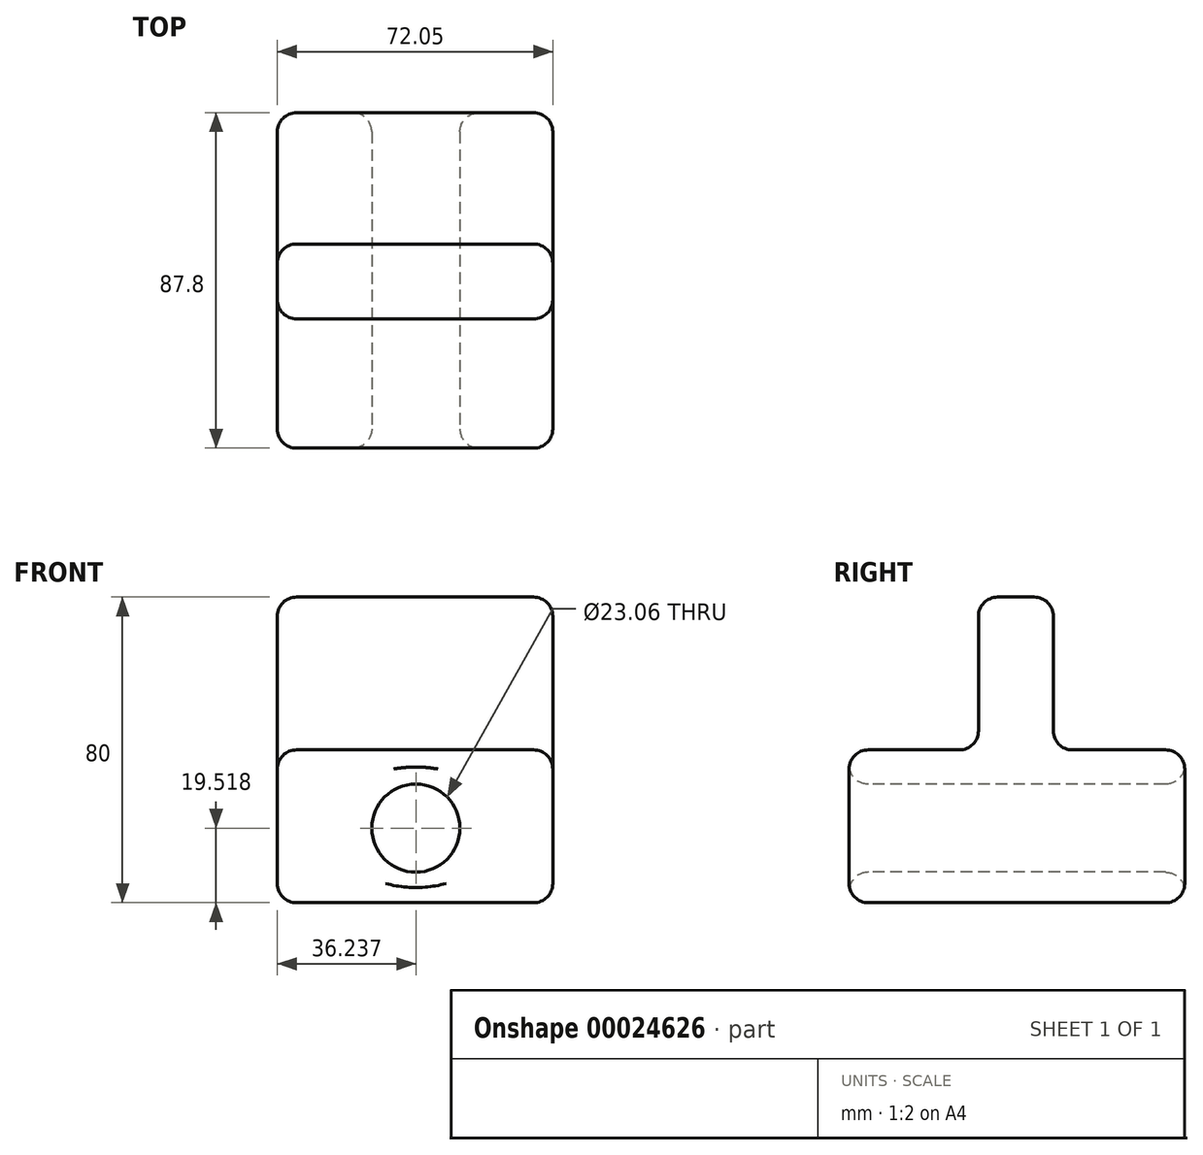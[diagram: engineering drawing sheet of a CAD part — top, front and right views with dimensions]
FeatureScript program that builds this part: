
annotation { "Feature Type Name" : "Feature", "Feature Type Description" : "" }
export const myFeature = defineFeature(function(context is Context, id is Id, definition is map)
    precondition{}
    {
        {
            var Q0;
            Q0=qCreatedBy(makeId("Top.planeOp"),FACE);
            var sketch = newSketch(context, id + "F0", { "sketchPlane" : qUnion([Q0])});
            skLineSegment(sketch, "E0.bottom", {"start": v(-59.89, -44.54) * mm, "end": v(12.16, -44.54) * mm});
            skLineSegment(sketch, "E0.top", {"start": v(-59.89, 43.26) * mm, "end": v(12.16, 43.26) * mm});
            skLineSegment(sketch, "E0.left", {"start": v(-59.89, -44.54) * mm, "end": v(-59.89, 43.26) * mm});
            skLineSegment(sketch, "E0.right", {"start": v(12.16, -44.54) * mm, "end": v(12.16, 43.26) * mm});
            skSolve(sketch);
        }
        {
            var Q0;
            Q0=makeQuery(id+"F0.imprint","IMPRINT",FACE,{"disambiguationData":[TD([[makeQuery(id+"F0.imprint","IMPRINT",EDGE,{"derivedFrom":sQuery(id+"F0.wireOp",EDGE,"E0.bottom")}),1.0]])]});
            extrude(context, id + "F1", {"entities" : qUnion([Q0]), "depth" : 40 * mm});
        }
        {
            var Q0;
            Q0=makeQuery(id+"F1.opExtrude","SWEPT_FACE",FACE,{"disambiguationData":[OSD([sQuery(id+"F0.wireOp",EDGE,"E0.bottom")])]});
            var sketch = newSketch(context, id + "F2", { "sketchPlane" : qUnion([Q0])});
            skCircle(sketch, "E1", {"center": v(-23.65, 19.52) * mm, "radius": 11.53 * mm});
            skSolve(sketch);
        }
        {
            var Q0;
            Q0=makeQuery(id+"F2.imprint","IMPRINT",FACE,{"disambiguationData":[TD([[makeQuery(id+"F2.imprint","IMPRINT",EDGE,{"derivedFrom":sQuery(id+"F2.wireOp",EDGE,"E1")}),1.0]])]});
            extrude(context, id + "F3", {"entities" : qUnion([Q0]), "operationType" : NewBodyOperationType.REMOVE, "endBound" : BoundingType.THROUGH_ALL, "oppositeDirection" : true, "depth" : 25 * mm});
        }
        {
            var Q0;
            Q0=makeQuery(id+"F1.opExtrude","CAP_FACE",FACE,{"disambiguationData":[OSD([sQuery(id+"F0.wireOp",EDGE,"E0.bottom"),sQuery(id+"F0.wireOp",EDGE,"E0.top"),sQuery(id+"F0.wireOp",EDGE,"E0.left"),sQuery(id+"F0.wireOp",EDGE,"E0.right")])],"isStart":false});
            var sketch = newSketch(context, id + "F4", { "sketchPlane" : qUnion([Q0])});
            skLineSegment(sketch, "E2.bottom", {"start": v(-59.89, -10.7) * mm, "end": v(12.16, -10.7) * mm});
            skLineSegment(sketch, "E2.top", {"start": v(-59.89, 8.88) * mm, "end": v(12.16, 8.88) * mm});
            skLineSegment(sketch, "E2.left", {"start": v(-59.89, -10.7) * mm, "end": v(-59.89, 8.88) * mm});
            skLineSegment(sketch, "E2.right", {"start": v(12.16, -10.7) * mm, "end": v(12.16, 8.88) * mm});
            skSolve(sketch);
        }
        {
            var Q0;
            Q0=makeQuery(id+"F4.imprint","IMPRINT",FACE,{"disambiguationData":[TD([[makeQuery(id+"F4.imprint","IMPRINT",EDGE,{"derivedFrom":sQuery(id+"F4.wireOp",EDGE,"E2.bottom")}),1.0]])]});
            extrude(context, id + "F5", {"entities" : qUnion([Q0]), "operationType" : NewBodyOperationType.ADD, "depth" : 40 * mm});
        }
        {
            var Q0;
            Q0=makeQuery(id+"F3.boolean.opBoolean","COPY",FACE,{"derivedFrom":makeQuery(id+"F3.opExtrude","SWEPT_FACE",FACE,{"disambiguationData":[OSD([sQuery(id+"F2.wireOp",EDGE,"E1")])]})});
            var Q1;
            Q1=makeQuery(id+"F1.opExtrude","SWEPT_FACE",FACE,{"disambiguationData":[OSD([sQuery(id+"F0.wireOp",EDGE,"E0.bottom")])]});
            var Q2;
            Q2=makeQuery(id+"F3.boolean.opBoolean","COPY",EDGE,{"derivedFrom":makeQuery(id+"F3.opExtrude","CAP_EDGE",EDGE,{"disambiguationData":[OSD([sQuery(id+"F2.wireOp",EDGE,"E1")])],"isStart":true})});
            var Q3;
            Q3=makeQuery(id+"F5.opExtrude","SWEPT_EDGE",EDGE,{"disambiguationData":[OSD([sQuery(id+"F0.wireOp",EDGE,"E0.left"),sQuery(id+"F4.wireOp",EDGE,"E2.bottom"),sQuery(id+"F4.wireOp",EDGE,"E2.left")])]});
            var Q4;
            Q4=makeQuery(id+"F5.opExtrude","SWEPT_FACE",FACE,{"disambiguationData":[OSD([sQuery(id+"F4.wireOp",EDGE,"E2.bottom")])]});
            var Q5;
            Q5=makeQuery(id+"F5.opExtrude","SWEPT_EDGE",EDGE,{"disambiguationData":[OSD([sQuery(id+"F0.wireOp",EDGE,"E0.right"),sQuery(id+"F4.wireOp",EDGE,"E2.bottom"),sQuery(id+"F4.wireOp",EDGE,"E2.right")])]});
            var Q6;
            Q6=makeQuery(id+"F5.opExtrude","CAP_FACE",FACE,{"disambiguationData":[OSD([sQuery(id+"F4.wireOp",EDGE,"E2.bottom"),sQuery(id+"F4.wireOp",EDGE,"E2.top"),sQuery(id+"F4.wireOp",EDGE,"E2.left"),sQuery(id+"F4.wireOp",EDGE,"E2.right")])],"isStart":false});
            var Q7;
            Q7=makeQuery(id+"F5.opExtrude","SWEPT_EDGE",EDGE,{"disambiguationData":[OSD([sQuery(id+"F0.wireOp",EDGE,"E0.right"),sQuery(id+"F4.wireOp",EDGE,"E2.top"),sQuery(id+"F4.wireOp",EDGE,"E2.right")])]});
            var Q8;
            Q8=makeQuery(id+"F5.opExtrude","CAP_EDGE",EDGE,{"disambiguationData":[OSD([sQuery(id+"F4.wireOp",EDGE,"E2.bottom")])],"isStart":false});
            var Q9;
            Q9=makeQuery(id+"F5.opExtrude","CAP_EDGE",EDGE,{"disambiguationData":[OSD([sQuery(id+"F4.wireOp",EDGE,"E2.bottom")])],"isStart":true});
            var Q10;
            Q10=makeQuery(id+"F5.opExtrude","CAP_EDGE",EDGE,{"disambiguationData":[OSD([sQuery(id+"F4.wireOp",EDGE,"E2.top")])],"isStart":false});
            var Q11;
            Q11=makeQuery(id+"F5.boolean.opBoolean","MERGE",FACE,{"derivedFrom":[makeQuery(id+"F1.opExtrude","SWEPT_FACE",FACE,{"disambiguationData":[OSD([sQuery(id+"F0.wireOp",EDGE,"E0.right")])]}),makeQuery(id+"F5.opExtrude","SWEPT_FACE",FACE,{"disambiguationData":[OSD([sQuery(id+"F4.wireOp",EDGE,"E2.right")])]})]});
            var Q12;
            {var subQ0=sQuery(id+"F0.wireOp",EDGE,"E0.bottom");var subQ1=sQuery(id+"F0.wireOp",EDGE,"E0.left");var subQ2=sQuery(id+"F0.wireOp",EDGE,"E0.right");Q12=makeQuery(id+"F5.boolean.opBoolean","SPLIT",FACE,{"disambiguationData":[TD([makeQuery(id+"F1.opExtrude","SWEPT_FACE",FACE,{"disambiguationData":[OSD([subQ0])]})])],"derivedFrom":makeQuery(id+"F1.opExtrude","CAP_FACE",FACE,{"disambiguationData":[OSD([subQ0,sQuery(id+"F0.wireOp",EDGE,"E0.top"),subQ1,subQ2])],"isStart":false})});}
            var Q13;
            Q13=makeQuery(id+"F1.opExtrude","SWEPT_EDGE",EDGE,{"disambiguationData":[OSD([sQuery(id+"F0.wireOp",EDGE,"E0.bottom"),sQuery(id+"F0.wireOp",EDGE,"E0.left")])]});
            var Q14;
            {var subQ0=sQuery(id+"F0.wireOp",EDGE,"E0.left");var subQ1=sQuery(id+"F0.wireOp",EDGE,"E0.bottom");Q14=makeQuery(id+"F5.boolean.opBoolean","SPLIT",EDGE,{"disambiguationData":[TD([makeQuery(id+"F1.opExtrude","SWEPT_FACE",FACE,{"disambiguationData":[OSD([subQ1])]})])],"derivedFrom":makeQuery(id+"F1.opExtrude","CAP_EDGE",EDGE,{"disambiguationData":[OSD([subQ0])],"isStart":false})});}
            var Q15;
            Q15=makeQuery(id+"F5.opExtrude","CAP_EDGE",EDGE,{"disambiguationData":[OSD([sQuery(id+"F4.wireOp",EDGE,"E2.left")])],"isStart":false});
            var Q16;
            {var subQ0=sQuery(id+"F0.wireOp",EDGE,"E0.top");var subQ1=sQuery(id+"F0.wireOp",EDGE,"E0.left");var subQ2=sQuery(id+"F0.wireOp",EDGE,"E0.right");Q16=makeQuery(id+"F5.boolean.opBoolean","SPLIT",FACE,{"disambiguationData":[TD([makeQuery(id+"F1.opExtrude","SWEPT_FACE",FACE,{"disambiguationData":[OSD([subQ0])]})])],"derivedFrom":makeQuery(id+"F1.opExtrude","CAP_FACE",FACE,{"disambiguationData":[OSD([sQuery(id+"F0.wireOp",EDGE,"E0.bottom"),subQ0,subQ1,subQ2])],"isStart":false})});}
            var Q17;
            {var subQ0=sQuery(id+"F0.wireOp",EDGE,"E0.right");var subQ1=sQuery(id+"F0.wireOp",EDGE,"E0.bottom");Q17=makeQuery(id+"F5.boolean.opBoolean","SPLIT",EDGE,{"disambiguationData":[TD([makeQuery(id+"F1.opExtrude","SWEPT_FACE",FACE,{"disambiguationData":[OSD([subQ1])]})])],"derivedFrom":makeQuery(id+"F1.opExtrude","CAP_EDGE",EDGE,{"disambiguationData":[OSD([subQ0])],"isStart":false})});}
            var Q18;
            Q18=makeQuery(id+"F5.opExtrude","CAP_EDGE",EDGE,{"disambiguationData":[OSD([sQuery(id+"F4.wireOp",EDGE,"E2.right")])],"isStart":false});
            var Q19;
            Q19=makeQuery(id+"F1.opExtrude","SWEPT_EDGE",EDGE,{"disambiguationData":[OSD([sQuery(id+"F0.wireOp",EDGE,"E0.top"),sQuery(id+"F0.wireOp",EDGE,"E0.right")])]});
            var Q20;
            {var subQ0=sQuery(id+"F0.wireOp",EDGE,"E0.right");var subQ1=sQuery(id+"F0.wireOp",EDGE,"E0.top");Q20=makeQuery(id+"F5.boolean.opBoolean","SPLIT",EDGE,{"disambiguationData":[TD([makeQuery(id+"F1.opExtrude","SWEPT_FACE",FACE,{"disambiguationData":[OSD([subQ1])]})])],"derivedFrom":makeQuery(id+"F1.opExtrude","CAP_EDGE",EDGE,{"disambiguationData":[OSD([subQ0])],"isStart":false})});}
            var Q21;
            Q21=makeQuery(id+"F1.opExtrude","CAP_EDGE",EDGE,{"disambiguationData":[OSD([sQuery(id+"F0.wireOp",EDGE,"E0.bottom")])],"isStart":true});
            var Q22;
            Q22=makeQuery(id+"F1.opExtrude","CAP_EDGE",EDGE,{"disambiguationData":[OSD([sQuery(id+"F0.wireOp",EDGE,"E0.bottom")])],"isStart":false});
            var Q23;
            Q23=makeQuery(id+"F1.opExtrude","CAP_EDGE",EDGE,{"disambiguationData":[OSD([sQuery(id+"F0.wireOp",EDGE,"E0.top")])],"isStart":false});
            var Q24;
            Q24=makeQuery(id+"F1.opExtrude","CAP_EDGE",EDGE,{"disambiguationData":[OSD([sQuery(id+"F0.wireOp",EDGE,"E0.right")])],"isStart":true});
            var Q25;
            Q25=makeQuery(id+"F3.boolean.opBoolean","INTERSECT",EDGE,{"derivedFrom":[makeQuery(id+"F1.opExtrude","SWEPT_FACE",FACE,{"disambiguationData":[OSD([sQuery(id+"F0.wireOp",EDGE,"E0.top")])]}),makeQuery(id+"F3.opExtrude","SWEPT_FACE",FACE,{"disambiguationData":[OSD([sQuery(id+"F2.wireOp",EDGE,"E1")])]})]});
            var Q26;
            Q26=makeQuery(id+"F1.opExtrude","SWEPT_FACE",FACE,{"disambiguationData":[OSD([sQuery(id+"F0.wireOp",EDGE,"E0.top")])]});
            var Q27;
            Q27=makeQuery(id+"F5.opExtrude","SWEPT_EDGE",EDGE,{"disambiguationData":[OSD([sQuery(id+"F0.wireOp",EDGE,"E0.left"),sQuery(id+"F4.wireOp",EDGE,"E2.top"),sQuery(id+"F4.wireOp",EDGE,"E2.left")])]});
            var Q28;
            Q28=makeQuery(id+"F5.opExtrude","SWEPT_FACE",FACE,{"disambiguationData":[OSD([sQuery(id+"F4.wireOp",EDGE,"E2.top")])]});
            var Q29;
            Q29=makeQuery(id+"F5.boolean.opBoolean","MERGE",FACE,{"derivedFrom":[makeQuery(id+"F1.opExtrude","SWEPT_FACE",FACE,{"disambiguationData":[OSD([sQuery(id+"F0.wireOp",EDGE,"E0.left")])]}),makeQuery(id+"F5.opExtrude","SWEPT_FACE",FACE,{"disambiguationData":[OSD([sQuery(id+"F4.wireOp",EDGE,"E2.left")])]})]});
            var Q30;
            Q30=makeQuery(id+"F5.opExtrude","CAP_EDGE",EDGE,{"disambiguationData":[OSD([sQuery(id+"F4.wireOp",EDGE,"E2.top")])],"isStart":true});
            var Q31;
            Q31=makeQuery(id+"F1.opExtrude","CAP_FACE",FACE,{"disambiguationData":[OSD([sQuery(id+"F0.wireOp",EDGE,"E0.bottom"),sQuery(id+"F0.wireOp",EDGE,"E0.top"),sQuery(id+"F0.wireOp",EDGE,"E0.left"),sQuery(id+"F0.wireOp",EDGE,"E0.right")])],"isStart":true});
            var Q32;
            Q32=makeQuery(id+"F1.opExtrude","SWEPT_EDGE",EDGE,{"disambiguationData":[OSD([sQuery(id+"F0.wireOp",EDGE,"E0.bottom"),sQuery(id+"F0.wireOp",EDGE,"E0.right")])]});
            var Q33;
            Q33=makeQuery(id+"F1.opExtrude","CAP_EDGE",EDGE,{"disambiguationData":[OSD([sQuery(id+"F0.wireOp",EDGE,"E0.top")])],"isStart":true});
            var Q34;
            Q34=makeQuery(id+"F1.opExtrude","CAP_EDGE",EDGE,{"disambiguationData":[OSD([sQuery(id+"F0.wireOp",EDGE,"E0.left")])],"isStart":true});
            var Q35;
            {var subQ0=sQuery(id+"F0.wireOp",EDGE,"E0.left");var subQ1=sQuery(id+"F0.wireOp",EDGE,"E0.top");Q35=makeQuery(id+"F5.boolean.opBoolean","SPLIT",EDGE,{"disambiguationData":[TD([makeQuery(id+"F1.opExtrude","SWEPT_FACE",FACE,{"disambiguationData":[OSD([subQ1])]})])],"derivedFrom":makeQuery(id+"F1.opExtrude","CAP_EDGE",EDGE,{"disambiguationData":[OSD([subQ0])],"isStart":false})});}
            var Q36;
            Q36=makeQuery(id+"F1.opExtrude","SWEPT_EDGE",EDGE,{"disambiguationData":[OSD([sQuery(id+"F0.wireOp",EDGE,"E0.top"),sQuery(id+"F0.wireOp",EDGE,"E0.left")])]});
            fillet(context, id + "F6", {"entities" : qUnion([Q0, Q1, Q2, Q3, Q4, Q5, Q6, Q7, Q8, Q9, Q10, Q11, Q12, Q13, Q14, Q15, Q16, Q17, Q18, Q19, Q20, Q21, Q22, Q23, Q24, Q25, Q26, Q27, Q28, Q29, Q30, Q31, Q32, Q33, Q34, Q35, Q36]), "radius" : 5 * mm, "tangentPropagation" : true, "allowEdgeOverflow" : false});
        }
    });
